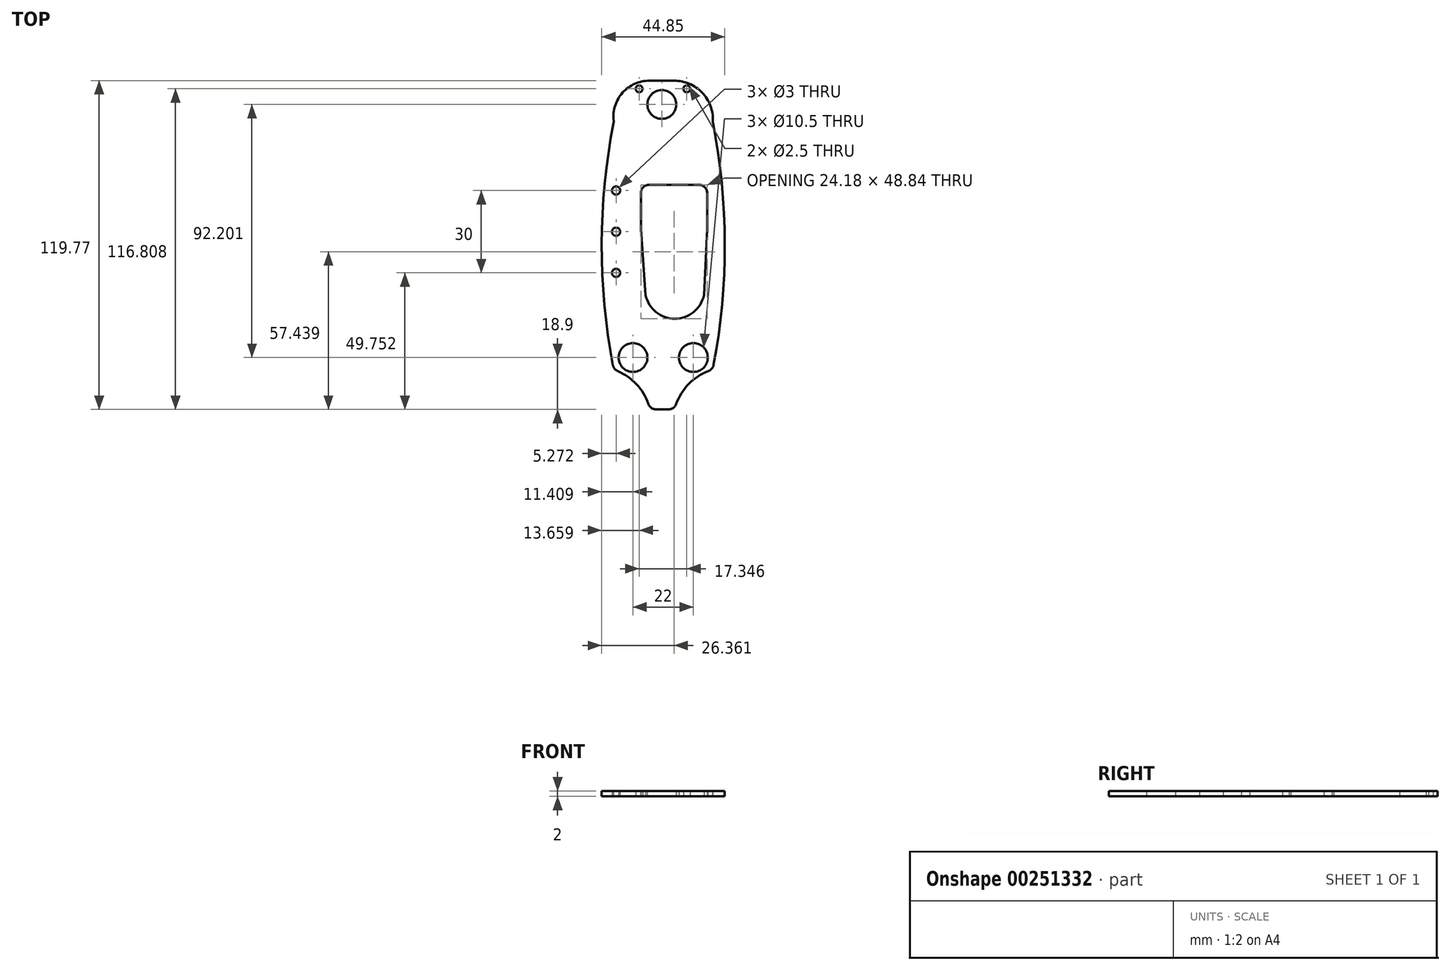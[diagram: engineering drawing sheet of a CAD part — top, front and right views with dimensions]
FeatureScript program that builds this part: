
annotation { "Feature Type Name" : "Feature", "Feature Type Description" : "" }
export const myFeature = defineFeature(function(context is Context, id is Id, definition is map)
    precondition{}
    {
        {
            var Q0;
            Q0=qCreatedBy(makeId("Top.planeOp"),FACE);
            var sketch = newSketch(context, id + "F0", { "sketchPlane" : qUnion([Q0])});
            skPoint(sketch, "E0.centerSnap0", {"position": v(-15.1, 30.97) * mm});
            skLineSegment(sketch, "E1.left", {"start": v(-18.17, -43.54) * mm, "end": v(-18.17, -45.33) * mm});
            skLineSegment(sketch, "E2", {"start": v(-0.67, 28.78) * mm, "end": v(-0.5, -52.83) * mm, "construction": true});
            skCircle(sketch, "E3", {"center": v(-12.27, 28.96) * mm, "radius": 1.75 * mm});
            skCircle(sketch, "E4.MirrorC", {"center": v(10.93, 29) * mm, "radius": 1.75 * mm});
            skLineSegment(sketch, "E5", {"start": v(17.87, -45.36) * mm, "end": v(17.87, -69.44) * mm});
            skLineSegment(sketch, "E6", {"start": v(17.87, -69.44) * mm, "end": v(-18.17, -69.41) * mm});
            skLineSegment(sketch, "E7", {"start": v(-18.17, -69.41) * mm, "end": v(-18.17, -45.33) * mm});
            skLineSegment(sketch, "E8.bottom", {"start": v(-9.77, 31.46) * mm, "end": v(-14.77, 31.46) * mm});
            skLineSegment(sketch, "E8.top", {"start": v(-9.77, 26.46) * mm, "end": v(-14.77, 26.46) * mm});
            skLineSegment(sketch, "E8.left", {"start": v(-9.77, 31.46) * mm, "end": v(-9.77, 26.46) * mm});
            skLineSegment(sketch, "E8.right", {"start": v(-14.77, 31.46) * mm, "end": v(-14.77, 26.46) * mm});
            skLineSegment(sketch, "E9.MirrorCS", {"start": v(8.42, 31.5) * mm, "end": v(8.44, 26.5) * mm});
            skLineSegment(sketch, "E10.MirrorCS", {"start": v(8.44, 26.5) * mm, "end": v(13.44, 26.52) * mm});
            skLineSegment(sketch, "E11.MirrorCS", {"start": v(13.42, 31.52) * mm, "end": v(13.44, 26.52) * mm});
            skLineSegment(sketch, "E12.MirrorCS", {"start": v(8.42, 31.5) * mm, "end": v(13.42, 31.52) * mm});
            skCircle(sketch, "E13", {"center": v(10.93, 8.5) * mm, "radius": 3 * mm});
            skCircle(sketch, "E14", {"center": v(10.93, 1.5) * mm, "radius": 3 * mm});
            skLineSegment(sketch, "E15", {"start": v(13.93, 8.5) * mm, "end": v(13.93, 1.5) * mm});
            skLineSegment(sketch, "E16", {"start": v(7.93, 8.5) * mm, "end": v(7.93, 1.5) * mm});
            skCircle(sketch, "E17", {"center": v(4.15, -12) * mm, "radius": 9.5 * mm});
            skLineSegment(sketch, "E18", {"start": v(-5.17, 51.46) * mm, "end": v(3.83, 51.46) * mm});
            skCircle(sketch, "E19", {"center": v(-0.67, 42.8) * mm, "radius": 5.25 * mm});
            skPoint(sketch, "E19.centerSnap0", {"position": v(-0.67, 51.46) * mm});
            skCircle(sketch, "E20", {"center": v(-11.17, -49.41) * mm, "radius": 5.25 * mm});
            skCircle(sketch, "E21", {"center": v(10.83, -49.41) * mm, "radius": 5.25 * mm});
            skCircle(sketch, "E22", {"center": v(-8.92, -64.41) * mm, "radius": 1.25 * mm});
            skCircle(sketch, "E23", {"center": v(8.08, -64.41) * mm, "radius": 1.25 * mm});
            skLineSegment(sketch, "E24", {"start": v(-5, -68.3) * mm, "end": v(4, -68.31) * mm});
            skArc(sketch, "E25", {"start": v(-5, -68.3) * mm, "mid": v(-9.7, -59.34) * mm, "end": v(-18.17, -53.82) * mm});
            skArc(sketch, "E26", {"start": v(17.87, -53.82) * mm, "mid": v(8.98, -59.2) * mm, "end": v(4, -68.31) * mm});
            skCircle(sketch, "E27", {"center": v(8.42, 48.5) * mm, "radius": 1.25 * mm});
            skCircle(sketch, "E28", {"center": v(-8.92, 48.5) * mm, "radius": 1.25 * mm});
            skArc(sketch, "E29", {"start": v(-5.17, 51.46) * mm, "mid": v(-15.09, 46.93) * mm, "end": v(-18.17, 36.46) * mm});
            skArc(sketch, "E30", {"start": v(17.9, 36.46) * mm, "mid": v(14.12, 47.01) * mm, "end": v(3.83, 51.46) * mm});
            skArc(sketch, "E31", {"start": v(17.87, -53.82) * mm, "mid": v(22.27, -8.68) * mm, "end": v(17.9, 36.46) * mm});
            skArc(sketch, "E32", {"start": v(-18.17, 36.46) * mm, "mid": v(-22.58, -8.68) * mm, "end": v(-18.17, -53.82) * mm});
            skLineSegment(sketch, "E33", {"start": v(14.67, -26.67) * mm, "end": v(15.87, -2.68) * mm});
            skLineSegment(sketch, "E34", {"start": v(-6.57, -26.67) * mm, "end": v(-8.28, -2.68) * mm});
            skLineSegment(sketch, "E35", {"start": v(-8.28, -2.68) * mm, "end": v(-8.32, 13.5) * mm});
            skLineSegment(sketch, "E36", {"start": v(-8.32, 13.5) * mm, "end": v(15.84, 13.55) * mm});
            skArc(sketch, "E37", {"start": v(-6.57, -26.67) * mm, "mid": v(4.05, -35.29) * mm, "end": v(14.67, -26.67) * mm});
            skLineSegment(sketch, "E38", {"start": v(15.87, -2.68) * mm, "end": v(15.84, 13.55) * mm});
            skCircle(sketch, "E39", {"center": v(-17.3, -3.56) * mm, "radius": 1.5 * mm});
            skCircle(sketch, "E40", {"center": v(-17.3, -18.56) * mm, "radius": 1.5 * mm});
            skCircle(sketch, "E41", {"center": v(-17.3, 11.44) * mm, "radius": 1.5 * mm});
            skSolve(sketch);
        }
        {
            var Q0;
            Q0=makeQuery(id+"F0.imprint","IMPRINT",FACE,{"disambiguationData":[TD([[makeQuery(id+"F0.imprint","IMPRINT",EDGE,{"derivedFrom":sQuery(id+"F0.wireOp",EDGE,"E8.bottom")}),-1.0]])]});
            var Q1;
            Q1=makeQuery(id+"F0.imprint","IMPRINT",FACE,{"disambiguationData":[TD([[makeQuery(id+"F0.imprint","IMPRINT",EDGE,{"derivedFrom":sQuery(id+"F0.wireOp",EDGE,"E3")}),-1.0]])]});
            var Q2;
            Q2=makeQuery(id+"F0.imprint","IMPRINT",FACE,{"disambiguationData":[TD([[makeQuery(id+"F0.imprint","IMPRINT",EDGE,{"derivedFrom":sQuery(id+"F0.wireOp",EDGE,"E3")}),1.0]])]});
            var Q3;
            Q3=makeQuery(id+"F0.imprint","IMPRINT",FACE,{"disambiguationData":[TD([[makeQuery(id+"F0.imprint","IMPRINT",EDGE,{"derivedFrom":sQuery(id+"F0.wireOp",EDGE,"E4.MirrorC")}),1.0]])]});
            var Q4;
            Q4=makeQuery(id+"F0.imprint","IMPRINT",FACE,{"disambiguationData":[TD([[makeQuery(id+"F0.imprint","IMPRINT",EDGE,{"derivedFrom":sQuery(id+"F0.wireOp",EDGE,"E4.MirrorC")}),-1.0]])]});
            extrude(context, id + "F1", {"entities" : qUnion([Q0, Q1, Q2, Q3, Q4]), "depth" : 2 * mm});
        }
        {
            var Q0;
            Q0=makeQuery(id+"F1.opExtrude","SWEPT_EDGE",EDGE,{"disambiguationData":[OSD([sQuery(id+"F0.wireOp",EDGE,"E24"),sQuery(id+"F0.wireOp",EDGE,"E26")])]});
            var Q1;
            Q1=makeQuery(id+"F1.opExtrude","SWEPT_EDGE",EDGE,{"disambiguationData":[OSD([sQuery(id+"F0.wireOp",EDGE,"E24"),sQuery(id+"F0.wireOp",EDGE,"E25")])]});
            var Q2;
            Q2=makeQuery(id+"F1.opExtrude","SWEPT_EDGE",EDGE,{"disambiguationData":[OSD([sQuery(id+"F0.wireOp",EDGE,"E35"),sQuery(id+"F0.wireOp",EDGE,"E36")])]});
            var Q3;
            Q3=makeQuery(id+"F1.opExtrude","SWEPT_EDGE",EDGE,{"disambiguationData":[OSD([sQuery(id+"F0.wireOp",EDGE,"E36"),sQuery(id+"F0.wireOp",EDGE,"E38")])]});
            var Q4;
            Q4=makeQuery(id+"F1.opExtrude","SWEPT_EDGE",EDGE,{"disambiguationData":[OSD([sQuery(id+"F0.wireOp",EDGE,"E30"),sQuery(id+"F0.wireOp",EDGE,"E31")])]});
            var Q5;
            Q5=makeQuery(id+"F1.opExtrude","SWEPT_EDGE",EDGE,{"disambiguationData":[OSD([sQuery(id+"F0.wireOp",EDGE,"E29"),sQuery(id+"F0.wireOp",EDGE,"E32")])]});
            var Q6;
            Q6=makeQuery(id+"F1.opExtrude","SWEPT_EDGE",EDGE,{"disambiguationData":[OSD([sQuery(id+"F0.wireOp",EDGE,"E5"),sQuery(id+"F0.wireOp",EDGE,"E26"),sQuery(id+"F0.wireOp",EDGE,"E31")])]});
            var Q7;
            Q7=makeQuery(id+"F1.opExtrude","SWEPT_EDGE",EDGE,{"disambiguationData":[OSD([sQuery(id+"F0.wireOp",EDGE,"E7"),sQuery(id+"F0.wireOp",EDGE,"E25"),sQuery(id+"F0.wireOp",EDGE,"E32")])]});
            fillet(context, id + "F2", {"entities" : qUnion([Q0, Q1, Q2, Q3, Q4, Q5, Q6, Q7]), "radius" : 3 * mm, "tangentPropagation" : true, "allowEdgeOverflow" : false});
        }
    });
